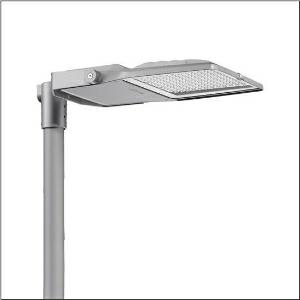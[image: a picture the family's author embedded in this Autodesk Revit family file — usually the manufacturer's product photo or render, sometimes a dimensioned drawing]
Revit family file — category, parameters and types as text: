
# Revit family: floodlight_fl_21_midi___pl64_5xa7781e4e3a_ded9
name_source: partatom
category: Lighting Fixtures
units: mm (PartAtom-declared; Revit-internal decimal feet)

## family parameters
Cut with Voids When Loaded = No
Host = Face
Light Source = No
Part Type = Normal
Room Calculation Point = No
Round Connector Dimension = Use Diameter
Shared = No

## types (1)
- --- (1 x LED, 27050 lm, 208.1 W, 4000K)
    Apparent Load = 208 VA
    CIE Flux Codes = 28 80 98 100 100
    Color Rendering = 70
    Color Temperature = 4000K
    Default Elevation = 1800 mm
    Description = Floodlight FL 21 midi, floodlight, primary light control with lens, of PMMA, primary optical cover: protective disc, of toughened safety glass, transparent, light distribution: PL64, light emission: direct distribution, installation type: surface-mounted, LED, High Power LED, rated luminous flux: 27.050lm, luminous efficacy: 129lm/W, light colour: 740, colour temperature: 4000K, control gear: ECG iQ, control: optimised constant luminous flux control (CLO 2.0), Desk-Remote (wireless, voltage-free reading and setting of iQ features in the workshop via application-optimized NFC function/RFID function), Light-Fading, Smart-Wire, Night-Set, Lumen-Switch, Temp-Guard, Auto-Match, with terminal, 6-pole, mains connection: 220..240V, AC, 50/60Hz, start of lifetime: 208W, end of lifetime: 227W, reduction: 90W, luminaire housing, of diecast aluminium, powder-coated, Siteco® metallic grey (DB 702S), corrosivity category C5 according to DIN EN ISO 12944, mast bracket, of steel, galvanised, powder-coated, Siteco® metallic grey (DB 702S), protection rating (complete): IP66, insulation class (complete): insulation class I (protective earthing), certification: CE, protection symbol: D, impact resistance: IK08, permissible operating ambient temperature: -40..+40°C, permissible operating ambient temperature for outdoor applications: -40..+50°C, standard: DIN EN 12944, packaging unit: 1 piece

Light Distribution: PL64
    Height = 76 mm
    Lamp = 1 x LED
    Lamp Light Flux = 27050 lm
    Lamp Power = 208.1 W
    Lamp count = 1
    Length = 657 mm
    Luminous efficacy = 130 lm/W
    Manufacturer = Siteco
    ModVariant = No
    Model = 5XA7781E4E3A
    Number of Poles = 1
    OnlyDefault = Yes
    Power Factor = 1
    Product Name = Floodlight FL 21 midi | PL64
    Product group = floodlight | pylon top
    ProductGroupID = 6101
    Protection Class = Protection class I
    Protection Degree = IP 66
    RLX_Detail_Level = 1
    RlxData = <blob elided: 153345 chars, md5=980701a5>
    Socket = socket
    Standby Power = 0 W
    System Light Flux = 27050 lm
    System Power = 208 W
    Type Comments = factory setting: luminous flux: 100 % | dim-lin: 254 | 710 mA
    Type Image = l_1007123.jpg
    URL = http://relux.com
    VarID = @adj_015689
    Voltage = 0 V
    Weight = 0.00 kg
    Width = 442 mm

## geometry (parser evidence)
native form markers: Blend x4, Sweep x12
no freeform markers — native parametric forms only
